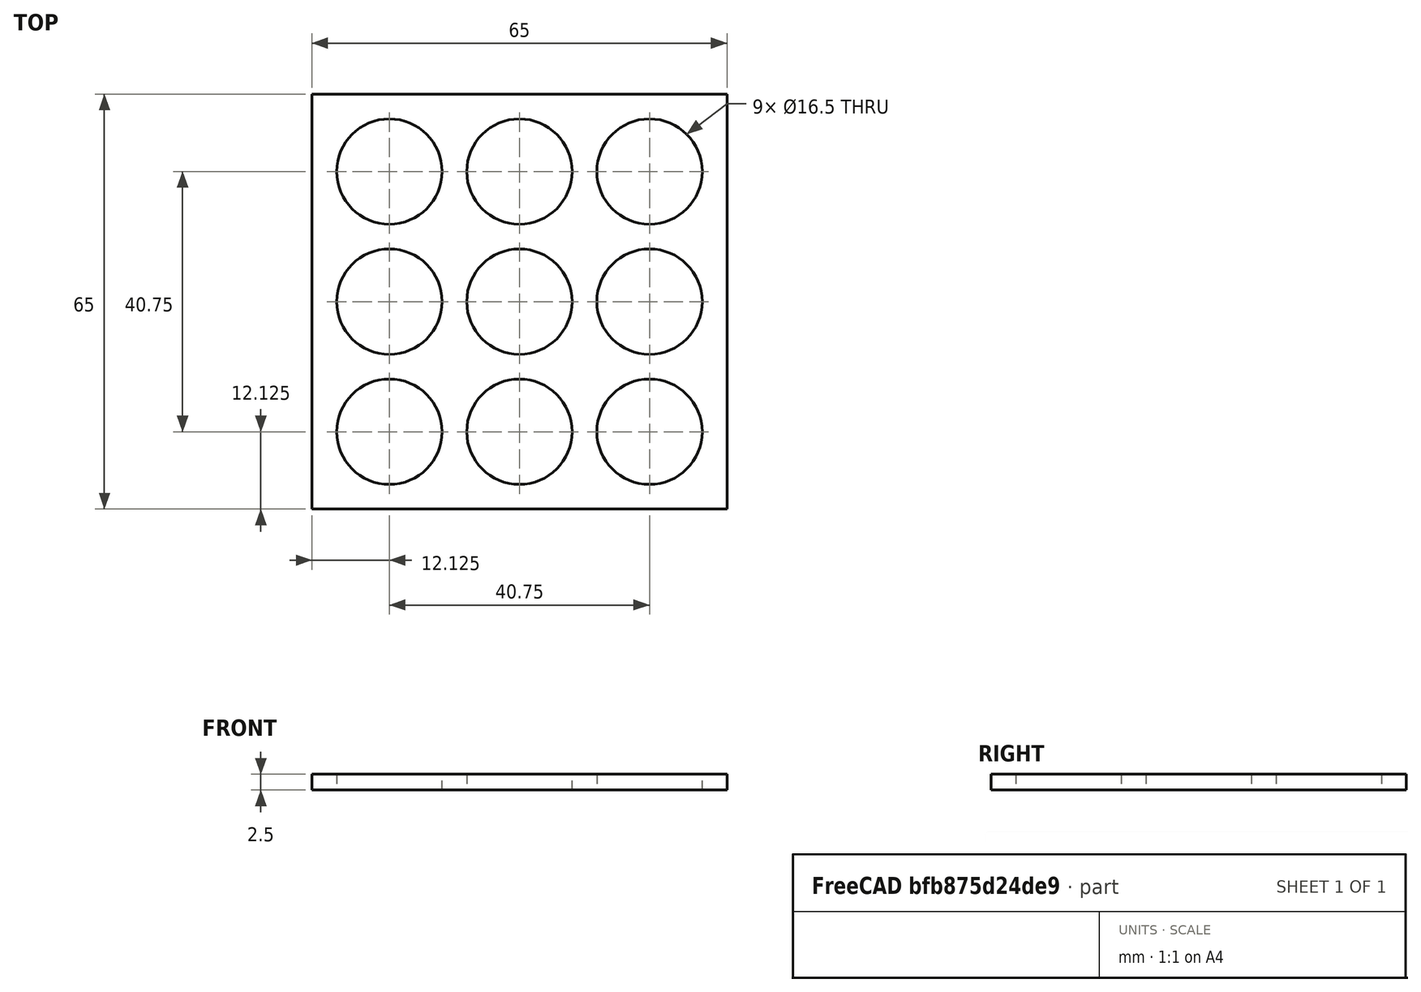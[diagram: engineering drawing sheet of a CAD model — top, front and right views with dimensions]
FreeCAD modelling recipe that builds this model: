
FCSTD DOCUMENT  (FreeCAD 0.19R)
Label: top
License: All rights reserved
LicenseURL: http://en.wikipedia.org/wiki/All_rights_reserved
objects: Sketcher::SketchObject×1, PartDesign::Pad×1, PartDesign::Body×1, Mesh::Feature×1
note: 4 computed .brp shape members not serialized (recipe doc carries the construction recipe); baked Part::Feature solids carry a one-line shape summary decoded from their .brp

FEATURE [Sketcher::SketchObject] Sketch
  FullyConstrained = true
  MapMode = 5
  Support = -> [XY_Plane]
  sketch-geometry (24):
    g0: LineSegment StartX=0 StartY=0 StartZ=0 EndX=65 EndY=0 EndZ=0
    g1: LineSegment StartX=65 StartY=0 StartZ=0 EndX=65 EndY=65 EndZ=0
    g2: LineSegment StartX=65 StartY=65 StartZ=0 EndX=0 EndY=65 EndZ=0
    g3: LineSegment StartX=0 StartY=65 StartZ=0 EndX=0 EndY=0 EndZ=0
    g4: Circle CenterX=12.125 CenterY=52.875 CenterZ=0 NormalX=0 NormalY=0 NormalZ=1 AngleXU=0 Radius=8.25
    g5: Circle CenterX=32.5 CenterY=52.875 CenterZ=0 NormalX=0 NormalY=0 NormalZ=1 AngleXU=0 Radius=8.25
    g6: Circle CenterX=52.875 CenterY=52.875 CenterZ=0 NormalX=0 NormalY=0 NormalZ=1 AngleXU=0 Radius=8.25
    g7: Circle CenterX=12.125 CenterY=32.5 CenterZ=0 NormalX=0 NormalY=0 NormalZ=1 AngleXU=0 Radius=8.25
    g8: Circle CenterX=32.5 CenterY=32.5 CenterZ=0 NormalX=0 NormalY=0 NormalZ=1 AngleXU=0 Radius=8.25
    g9: Circle CenterX=52.875 CenterY=32.5 CenterZ=0 NormalX=0 NormalY=0 NormalZ=1 AngleXU=0 Radius=8.25
    g10: Circle CenterX=12.125 CenterY=12.125 CenterZ=0 NormalX=0 NormalY=0 NormalZ=1 AngleXU=0 Radius=8.25
    g11: Circle CenterX=32.5 CenterY=12.125 CenterZ=0 NormalX=0 NormalY=0 NormalZ=1 AngleXU=0 Radius=8.25
    g12: Circle CenterX=52.875 CenterY=12.125 CenterZ=0 NormalX=0 NormalY=0 NormalZ=1 AngleXU=0 Radius=8.25
    g13: LineSegment StartX=12.125 StartY=65 StartZ=0 EndX=12.125 EndY=0 EndZ=0
    g14: LineSegment StartX=32.5 StartY=65 StartZ=0 EndX=32.5 EndY=0 EndZ=0
    g15: LineSegment StartX=52.875 StartY=65 StartZ=0 EndX=52.875 EndY=0 EndZ=0
    g16: LineSegment StartX=0 StartY=52.875 StartZ=0 EndX=65 EndY=52.875 EndZ=0
    g17: LineSegment StartX=0 StartY=32.5 StartZ=0 EndX=65 EndY=32.5 EndZ=0
    g18: LineSegment StartX=0 StartY=12.125 StartZ=0 EndX=65 EndY=12.125 EndZ=0
    g19: GeomPoint X=40.75 Y=32.5 Z=0
    g20: GeomPoint X=24.25 Y=32.5 Z=0
    g21: GeomPoint X=32.5 Y=40.75 Z=0
    g22: GeomPoint X=32.5 Y=24.25 Z=0
    g23: GeomPoint X=3.875 Y=52.875 Z=0
  constraints (66):
    c: Coincident(g0,g1)
    c: Coincident(g1,g2)
    c: Coincident(g2,g3)
    c: Coincident(g3,g0)
    c: Horizontal(g0)
    c: Horizontal(g2)
    c: Vertical(g1)
    c: Vertical(g3)
    c: Coincident(g0,g-1)
    c: DistanceX(g2,g2) = 65
    c: DistanceY(g1,g1) = 65
    c: Diameter(g5) = 16.5
    c: Equal(g5,g4)
    c: Equal(g5,g6)
    c: Equal(g5,g9)
    c: Equal(g5,g8)
    c: Equal(g5,g7)
    c: Equal(g5,g10)
    c: Equal(g5,g11)
    c: Equal(g5,g12)
    c: PointOnObject(g13,g0)
    c: Vertical(g13)
    c: PointOnObject(g14,g0)
    c: Vertical(g14)
    c: PointOnObject(g15,g0)
    c: Vertical(g15)
    c: Symmetric(g1,g2,g14)
    c: PointOnObject(g16,g1)
    c: Horizontal(g16)
    c: PointOnObject(g17,g1)
    c: Horizontal(g17)
    c: PointOnObject(g18,g1)
    c: Horizontal(g18)
    c: Symmetric(g2,g0,g17)
    c: PointOnObject(g8,g17)
    c: PointOnObject(g8,g14)
    c: PointOnObject(g19,g8)
    c: PointOnObject(g19,g17)
    c: Symmetric(g17,g19,g9)
    c: PointOnObject(g20,g8)
    c: PointOnObject(g20,g17)
    c: Symmetric(g17,g20,g7)
    c: PointOnObject(g21,g8)
    c: PointOnObject(g22,g8)
    c: PointOnObject(g21,g14)
    c: PointOnObject(g22,g14)
    c: Symmetric(g21,g14,g5)
    c: Symmetric(g22,g14,g11)
    c: PointOnObject(g5,g16)
    c: PointOnObject(g11,g18)
    c: PointOnObject(g16,g3)
    c: PointOnObject(g18,g3)
    c: PointOnObject(g15,g2)
    c: PointOnObject(g13,g2)
    c: PointOnObject(g9,g15)
    c: PointOnObject(g7,g13)
    c: PointOnObject(g4,g16)
    c: PointOnObject(g4,g13)
    c: PointOnObject(g6,g16)
    c: PointOnObject(g6,g15)
    c: PointOnObject(g12,g18)
    c: PointOnObject(g12,g15)
    c: PointOnObject(g10,g18)
    c: PointOnObject(g10,g13)
    c: PointOnObject(g23,g4)
    c: PointOnObject(g23,g16)
FEATURE [PartDesign::Pad] Pad
  Direction = (1,1,1)
  Length = 2.5
  Length2 = 100
  Profile = -> Sketch
  Type = 0
FEATURE [PartDesign::Body] Body
  Group = -> [Sketch,Pad]
  Origin = -> Origin
  Tip = -> Pad
FEATURE [Mesh::Feature] Mesh  label="Body (Meshed)"
